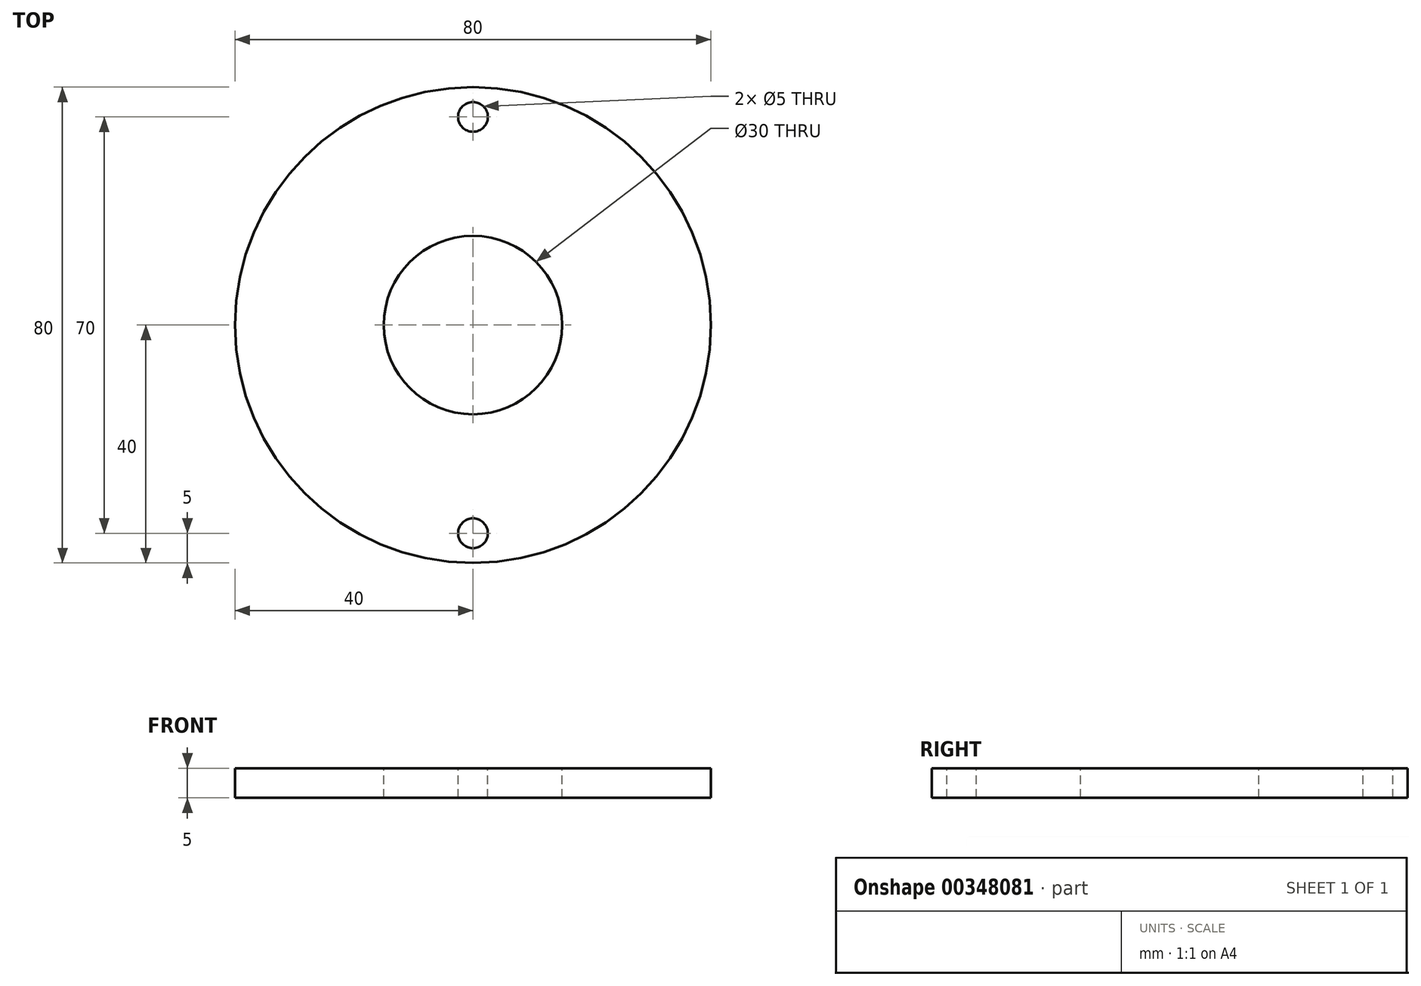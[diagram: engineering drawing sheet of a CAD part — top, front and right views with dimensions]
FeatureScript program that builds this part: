
annotation { "Feature Type Name" : "Feature", "Feature Type Description" : "" }
export const myFeature = defineFeature(function(context is Context, id is Id, definition is map)
    precondition{}
    {
        {
            var Q0;
            Q0=qCreatedBy(makeId("Top.planeOp"),FACE);
            var sketch = newSketch(context, id + "F0", { "sketchPlane" : qUnion([Q0])});
            skCircle(sketch, "E0", {"center": v(0, 0) * mm, "radius": 40 * mm});
            skLineSegment(sketch, "E1", {"start": v(0, 40) * mm, "end": v(0, 35) * mm});
            skLineSegment(sketch, "E2", {"start": v(0, -40) * mm, "end": v(0, -35) * mm});
            skCircle(sketch, "E3", {"center": v(0, 35) * mm, "radius": 2.5 * mm});
            skCircle(sketch, "E4", {"center": v(0, -35) * mm, "radius": 2.5 * mm});
            skLineSegment(sketch, "E5", {"start": v(0, 0) * mm, "end": v(-8.5, 0) * mm});
            skLineSegment(sketch, "E6", {"start": v(0, 0) * mm, "end": v(8.5, 0) * mm});
            skLineSegment(sketch, "E7", {"start": v(-8.5, 39.09) * mm, "end": v(-8.5, -39.09) * mm});
            skLineSegment(sketch, "E8", {"start": v(8.5, 39.09) * mm, "end": v(8.5, -39.09) * mm});
            skCircle(sketch, "E9", {"center": v(0, 35) * mm, "radius": 1.5 * mm});
            skCircle(sketch, "E10", {"center": v(0, -35) * mm, "radius": 1.5 * mm});
            skSolve(sketch);
        }
        {
            var Q0;
            {var subQ0=sQuery(id+"F0.wireOp",EDGE,"E7");var subQ1=sQuery(id+"F0.wireOp",EDGE,"E0");var subQ2=makeQuery(id+"F0.imprint","INTERSECT",VERTEX,{"disambiguationData":[OD(0.0)],"derivedFrom":[subQ1,subQ0]});Q0=makeQuery(id+"F0.imprint","IMPRINT",FACE,{"disambiguationData":[TD([[makeQuery(id+"F0.imprint","IMPRINT",EDGE,{"disambiguationData":[TD([[subQ2,-1.0]])],"derivedFrom":subQ1}),1.0]])]});}
            var Q1;
            Q1=makeQuery(id+"F0.imprint","IMPRINT",FACE,{"disambiguationData":[TD([[makeQuery(id+"F0.imprint","IMPRINT",EDGE,{"derivedFrom":sQuery(id+"F0.wireOp",EDGE,"E4")}),-1.0]])]});
            var Q2;
            Q2=makeQuery(id+"F0.imprint","IMPRINT",FACE,{"disambiguationData":[TD([[makeQuery(id+"F0.imprint","IMPRINT",EDGE,{"derivedFrom":sQuery(id+"F0.wireOp",EDGE,"E3")}),-1.0]])]});
            var Q3;
            {var subQ0=sQuery(id+"F0.wireOp",EDGE,"E8");var subQ1=sQuery(id+"F0.wireOp",EDGE,"E0");var subQ2=makeQuery(id+"F0.imprint","INTERSECT",VERTEX,{"disambiguationData":[OD(0.0)],"derivedFrom":[subQ1,subQ0]});Q3=makeQuery(id+"F0.imprint","IMPRINT",FACE,{"disambiguationData":[TD([[makeQuery(id+"F0.imprint","IMPRINT",EDGE,{"disambiguationData":[TD([[subQ2,1.0]])],"derivedFrom":subQ1}),1.0]])]});}
            var Q4;
            Q4=makeQuery(id+"F0.imprint","IMPRINT",FACE,{"disambiguationData":[TD([[makeQuery(id+"F0.imprint","IMPRINT",EDGE,{"derivedFrom":sQuery(id+"F0.wireOp",EDGE,"E3")}),1.0]])]});
            var Q5;
            Q5=makeQuery(id+"F0.imprint","IMPRINT",FACE,{"disambiguationData":[TD([[makeQuery(id+"F0.imprint","IMPRINT",EDGE,{"derivedFrom":sQuery(id+"F0.wireOp",EDGE,"E4")}),1.0]])]});
            extrude(context, id + "F1", {"entities" : qUnion([Q0, Q1, Q2, Q3, Q4, Q5]), "depth" : 5 * mm});
        }
        {
            var Q0;
            Q0=makeQuery(id+"F1.opExtrude","CAP_FACE",FACE,{"disambiguationData":[OSD([sQuery(id+"F0.wireOp",EDGE,"E0"),sQuery(id+"F0.wireOp",EDGE,"E9"),sQuery(id+"F0.wireOp",EDGE,"E10")])],"isStart":false});
            var sketch = newSketch(context, id + "F2", { "sketchPlane" : qUnion([Q0])});
            skCircle(sketch, "E11", {"center": v(0, 35) * mm, "radius": 2.5 * mm});
            skCircle(sketch, "E12", {"center": v(0, -35) * mm, "radius": 2.5 * mm});
            skSolve(sketch);
        }
        {
            var Q0;
            Q0=makeQuery(id+"F2.imprint","IMPRINT",FACE,{"disambiguationData":[TD([[makeQuery(id+"F2.imprint","IMPRINT",EDGE,{"derivedFrom":sQuery(id+"F2.wireOp",EDGE,"E11")}),1.0]])]});
            var Q1;
            Q1=makeQuery(id+"F2.imprint","IMPRINT",FACE,{"disambiguationData":[TD([[makeQuery(id+"F2.imprint","IMPRINT",EDGE,{"derivedFrom":sQuery(id+"F2.wireOp",EDGE,"E12")}),1.0]])]});
            extrude(context, id + "F3", {"entities" : qUnion([Q0, Q1]), "operationType" : NewBodyOperationType.REMOVE, "oppositeDirection" : true, "depth" : 2 * mm});
        }
        {
            var Q0;
            Q0=makeQuery(id+"F1.opExtrude","CAP_FACE",FACE,{"disambiguationData":[OSD([sQuery(id+"F0.wireOp",EDGE,"E0"),sQuery(id+"F0.wireOp",EDGE,"E9"),sQuery(id+"F0.wireOp",EDGE,"E10")])],"isStart":false});
            var sketch = newSketch(context, id + "F4", { "sketchPlane" : qUnion([Q0])});
            skCircle(sketch, "E13", {"center": v(0, 0) * mm, "radius": 15 * mm});
            skSolve(sketch);
        }
        {
            var Q0;
            Q0=makeQuery(id+"F4.imprint","IMPRINT",FACE,{"disambiguationData":[TD([[makeQuery(id+"F4.imprint","IMPRINT",EDGE,{"derivedFrom":sQuery(id+"F4.wireOp",EDGE,"E13")}),1.0]])]});
            extrude(context, id + "F5", {"entities" : qUnion([Q0]), "operationType" : NewBodyOperationType.REMOVE, "oppositeDirection" : true, "depth" : 25 * mm});
        }
        {
            var Q0;
            Q0=makeQuery(id+"F3.boolean.opBoolean","COPY",FACE,{"derivedFrom":makeQuery(id+"F3.opExtrude","CAP_FACE",FACE,{"disambiguationData":[OSD([sQuery(id+"F0.wireOp",EDGE,"E9"),sQuery(id+"F2.wireOp",EDGE,"E11")])],"isStart":false})});
            var Q1;
            Q1=makeQuery(id+"F3.boolean.opBoolean","COPY",FACE,{"derivedFrom":makeQuery(id+"F3.opExtrude","CAP_FACE",FACE,{"disambiguationData":[OSD([sQuery(id+"F0.wireOp",EDGE,"E10"),sQuery(id+"F2.wireOp",EDGE,"E12")])],"isStart":false})});
            extrude(context, id + "F6", {"entities" : qUnion([Q0, Q1]), "operationType" : NewBodyOperationType.REMOVE, "oppositeDirection" : true, "depth" : 25 * mm});
        }
    });
